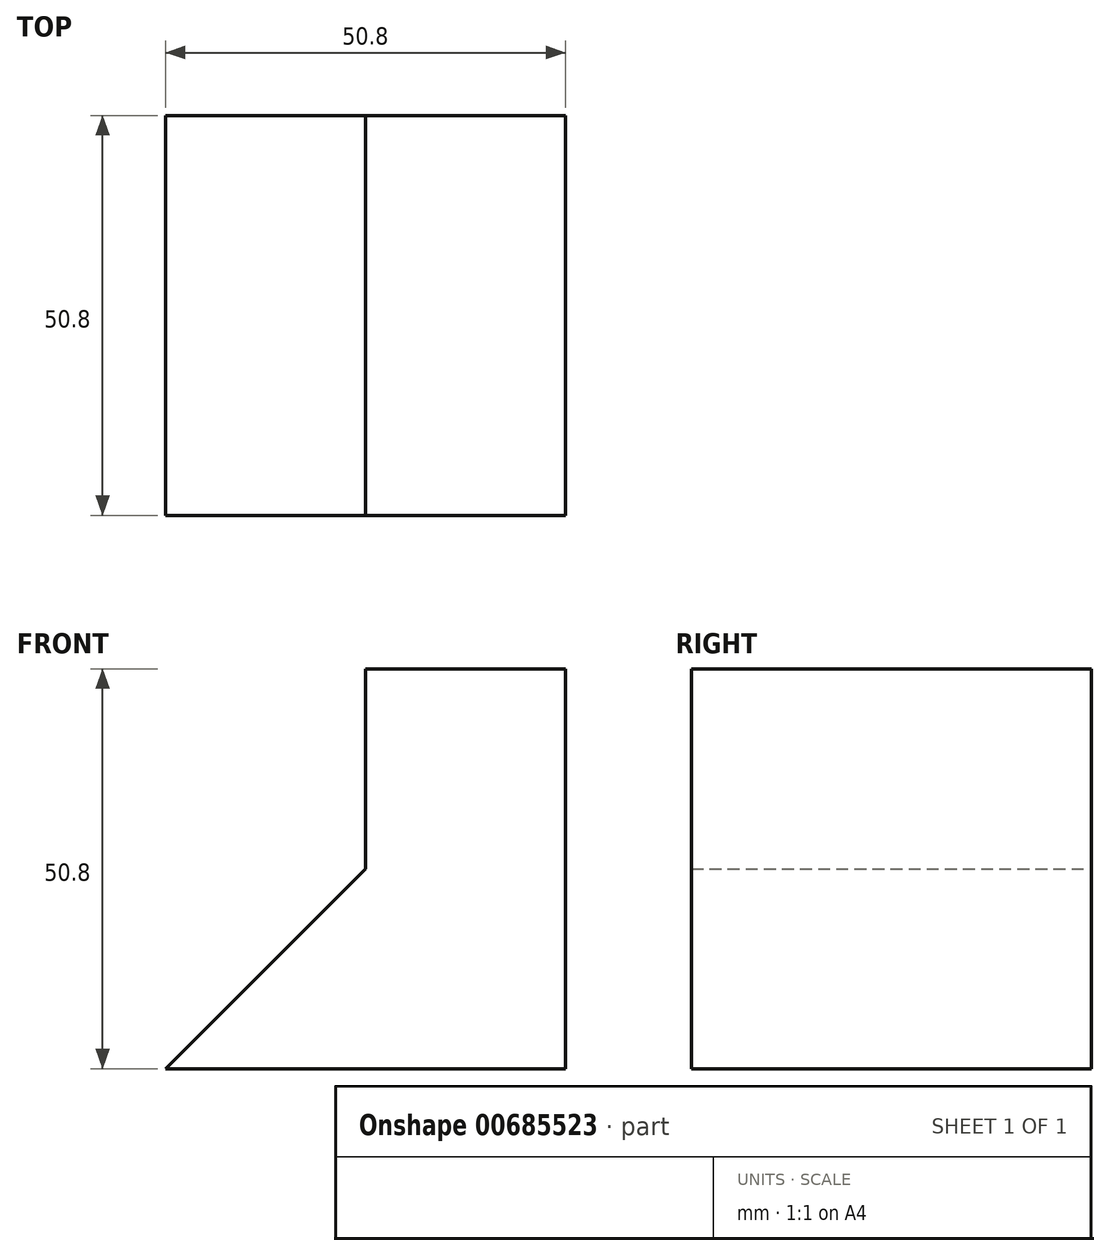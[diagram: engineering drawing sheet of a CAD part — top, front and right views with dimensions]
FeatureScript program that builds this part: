
annotation { "Feature Type Name" : "Feature", "Feature Type Description" : "" }
export const myFeature = defineFeature(function(context is Context, id is Id, definition is map)
    precondition{}
    {
        {
            var Q0;
            Q0=qCreatedBy(makeId("Front.planeOp"),FACE);
            var sketch = newSketch(context, id + "F0", { "sketchPlane" : qUnion([Q0])});
            skLineSegment(sketch, "E0", {"start": v(0, 0) * mm, "end": v(0, -50.8) * mm});
            skLineSegment(sketch, "E1", {"start": v(0, -50.8) * mm, "end": v(-50.8, -50.8) * mm});
            skLineSegment(sketch, "E2", {"start": v(0, 0) * mm, "end": v(-25.4, 0) * mm});
            skLineSegment(sketch, "E3", {"start": v(-25.4, 0) * mm, "end": v(-25.4, -25.4) * mm});
            skLineSegment(sketch, "E4", {"start": v(-25.4, -25.4) * mm, "end": v(-50.8, -50.8) * mm});
            skSolve(sketch);
        }
        {
            var Q0;
            Q0=makeQuery(id+"F0.imprint","IMPRINT",FACE,{"disambiguationData":[TD([[makeQuery(id+"F0.imprint","IMPRINT",EDGE,{"derivedFrom":sQuery(id+"F0.wireOp",EDGE,"E0")}),-1.0]])]});
            extrude(context, id + "F1", {"entities" : qUnion([Q0]), "depth" : 50.8 * mm, "offsetDistance" : 25.4 * mm});
        }
    });
